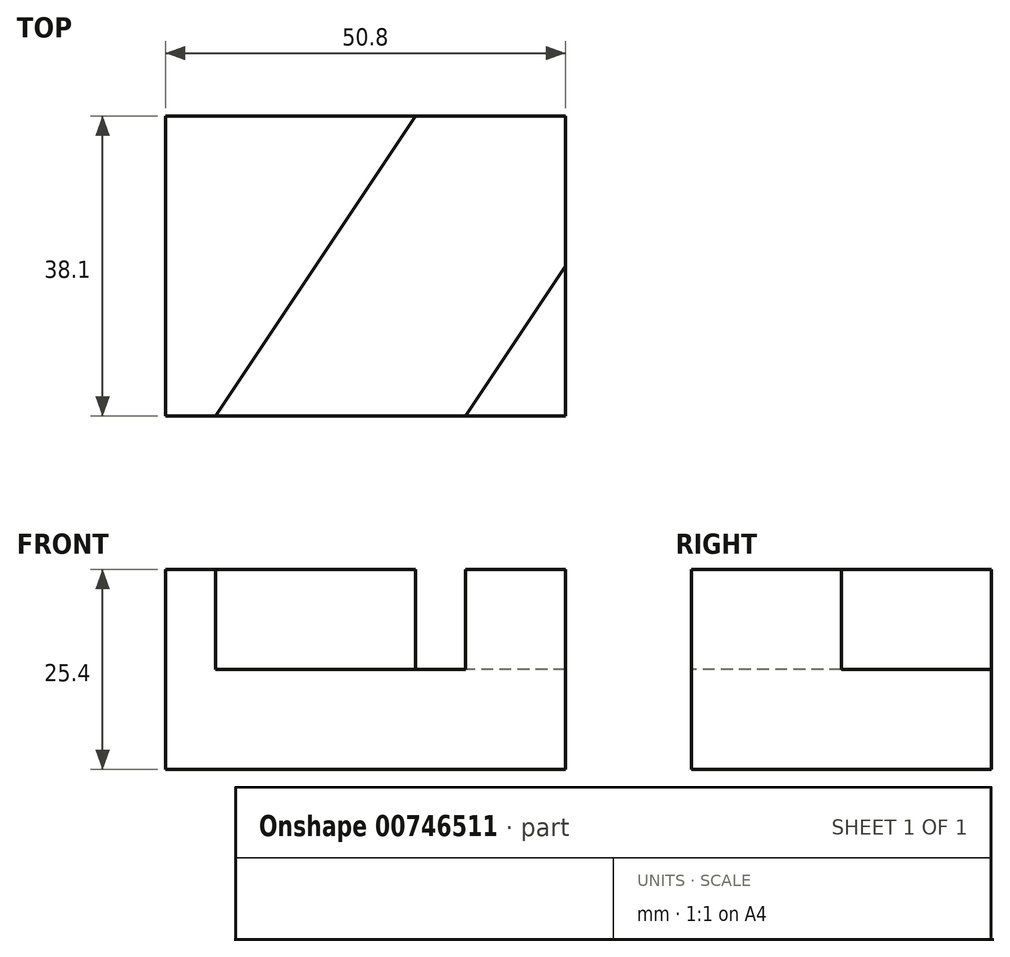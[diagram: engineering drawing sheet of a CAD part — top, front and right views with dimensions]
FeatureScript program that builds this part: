
annotation { "Feature Type Name" : "Feature", "Feature Type Description" : "" }
export const myFeature = defineFeature(function(context is Context, id is Id, definition is map)
    precondition{}
    {
        {
            var Q0;
            Q0=qCreatedBy(makeId("Front.planeOp"),FACE);
            var sketch = newSketch(context, id + "F0", { "sketchPlane" : qUnion([Q0])});
            skLineSegment(sketch, "E0", {"start": v(0, 0) * mm, "end": v(50.8, 0) * mm});
            skLineSegment(sketch, "E1", {"start": v(50.8, 0) * mm, "end": v(50.8, 25.4) * mm});
            skLineSegment(sketch, "E2", {"start": v(50.8, 25.4) * mm, "end": v(0, 25.4) * mm});
            skLineSegment(sketch, "E3", {"start": v(0, 25.4) * mm, "end": v(0, 0) * mm});
            skSolve(sketch);
        }
        {
            var Q0;
            Q0=makeQuery(id+"F0.imprint","IMPRINT",FACE,{"disambiguationData":[TD([[makeQuery(id+"F0.imprint","IMPRINT",EDGE,{"derivedFrom":sQuery(id+"F0.wireOp",EDGE,"E0")}),1.0]])]});
            extrude(context, id + "F1", {"entities" : qUnion([Q0]), "depth" : 38.1 * mm, "offsetDistance" : 25.4 * mm});
        }
        {
            var Q0;
            Q0=makeQuery(id+"F1.opExtrude","SWEPT_FACE",FACE,{"disambiguationData":[OSD([sQuery(id+"F0.wireOp",EDGE,"E2")])]});
            var sketch = newSketch(context, id + "F2", { "sketchPlane" : qUnion([Q0])});
            skLineSegment(sketch, "E4", {"start": v(6.35, -38.1) * mm, "end": v(31.75, 0) * mm});
            skLineSegment(sketch, "E5", {"start": v(31.75, 0) * mm, "end": v(0, 0) * mm});
            skLineSegment(sketch, "E6", {"start": v(50.8, -19.05) * mm, "end": v(38.1, -38.1) * mm});
            skLineSegment(sketch, "E7", {"start": v(38.1, -38.1) * mm, "end": v(50.8, -38.1) * mm});
            skLineSegment(sketch, "E8", {"start": v(50.8, -38.1) * mm, "end": v(50.8, -22.17) * mm});
            skLineSegment(sketch, "E9", {"start": v(50.8, -22.17) * mm, "end": v(50.8, -19.05) * mm});
            skLineSegment(sketch, "E10", {"start": v(6.35, -38.1) * mm, "end": v(0, -38.1) * mm});
            skLineSegment(sketch, "E11", {"start": v(0, 0) * mm, "end": v(0, -38.1) * mm});
            skSolve(sketch);
        }
        {
            var Q0;
            Q0=makeQuery(id+"F2.imprint","IMPRINT",FACE,{"disambiguationData":[TD([[makeQuery(id+"F2.imprint","IMPRINT",EDGE,{"derivedFrom":sQuery(id+"F2.wireOp",EDGE,"E4")}),1.0]])]});
            extrude(context, id + "F3", {"entities" : qUnion([Q0]), "operationType" : NewBodyOperationType.REMOVE, "oppositeDirection" : true, "depth" : 12.7 * mm, "offsetDistance" : 25.4 * mm});
        }
        {
            var Q0;
            Q0=makeQuery(id+"F1.opExtrude","SWEPT_FACE",FACE,{"disambiguationData":[OSD([sQuery(id+"F0.wireOp",EDGE,"E2")])]});
            var sketch = newSketch(context, id + "F4", { "sketchPlane" : qUnion([Q0])});
            skLineSegment(sketch, "E12", {"start": v(50.8, -19.05) * mm, "end": v(38.1, -38.1) * mm});
            skLineSegment(sketch, "E13", {"start": v(38.1, -38.1) * mm, "end": v(50.8, -38.1) * mm});
            skLineSegment(sketch, "E14", {"start": v(50.8, -38.1) * mm, "end": v(50.8, -19.05) * mm});
            skSolve(sketch);
        }
        {
            var Q0;
            Q0=makeQuery(id+"F3.boolean.opBoolean","COPY",FACE,{"derivedFrom":makeQuery(id+"F3.opExtrude","CAP_FACE",FACE,{"disambiguationData":[OSD([sQuery(id+"F2.wireOp",EDGE,"E4"),sQuery(id+"F2.wireOp",EDGE,"E10"),sQuery(id+"F2.wireOp",EDGE,"E5"),sQuery(id+"F2.wireOp",EDGE,"E11")])],"isStart":false})});
            extrude(context, id + "F5", {"entities" : qUnion([Q0]), "operationType" : NewBodyOperationType.ADD, "depth" : 12.7 * mm, "offsetDistance" : 25.4 * mm});
        }
        {
            var Q0;
            {var subQ4=sQuery(id+"F4.wireOp",EDGE,"E12");Q0=makeQuery(id+"F4.imprint","IMPRINT",FACE,{"disambiguationData":[TD([[makeQuery(id+"F4.imprint","IMPRINT",EDGE,{"derivedFrom":subQ4}),-1.0]])]});}
            extrude(context, id + "F6", {"entities" : qUnion([Q0]), "operationType" : NewBodyOperationType.REMOVE, "oppositeDirection" : true, "depth" : 12.7 * mm, "offsetDistance" : 25.4 * mm});
        }
    });
